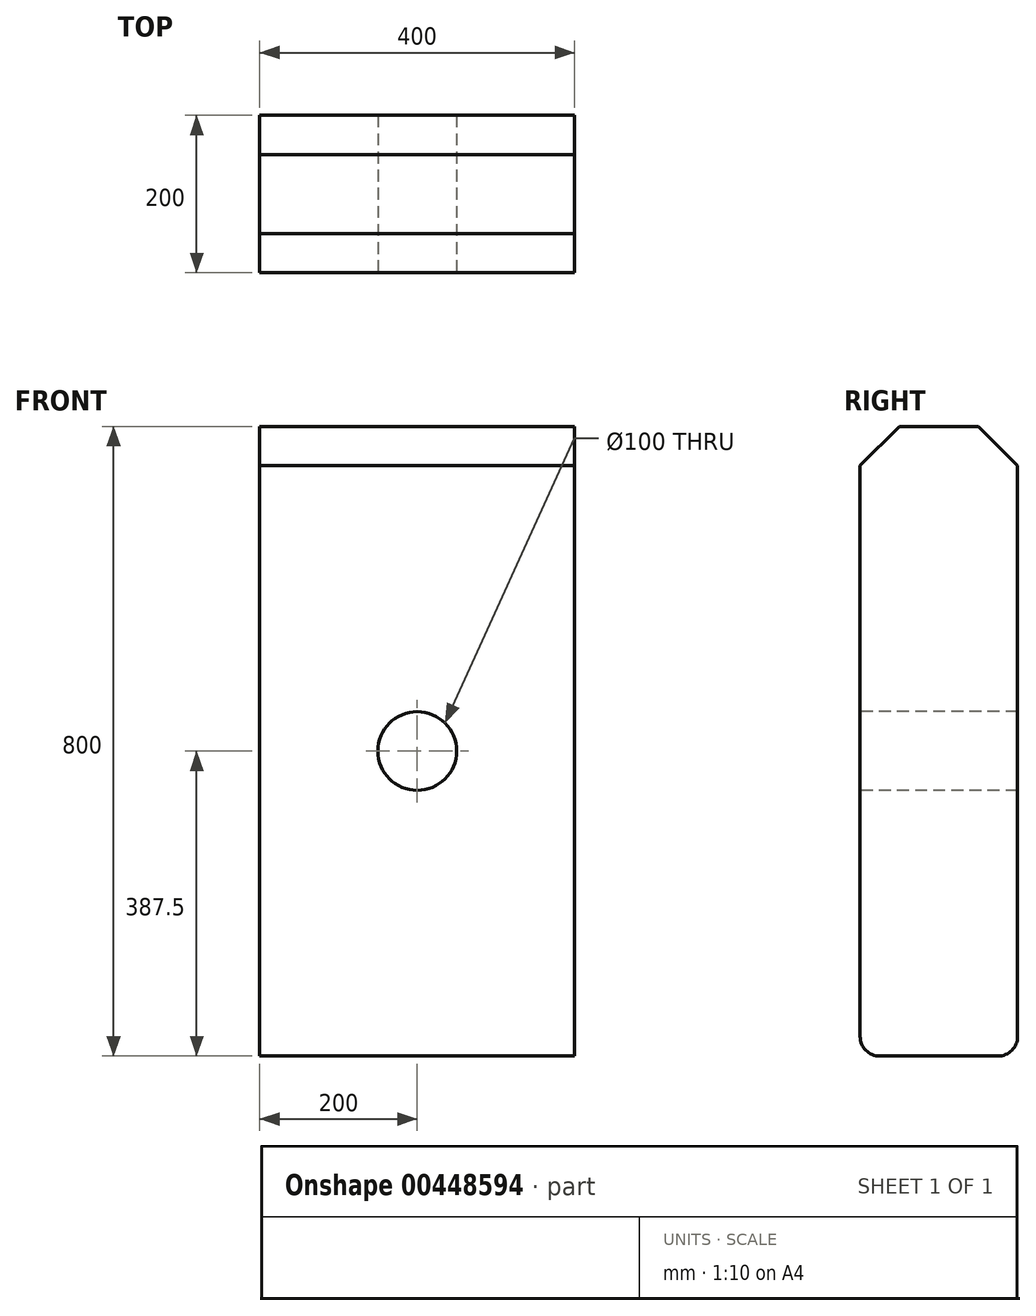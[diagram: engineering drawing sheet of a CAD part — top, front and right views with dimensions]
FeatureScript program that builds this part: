
annotation { "Feature Type Name" : "Feature", "Feature Type Description" : "" }
export const myFeature = defineFeature(function(context is Context, id is Id, definition is map)
    precondition{}
    {
        {
            var Q0;
            Q0=qCreatedBy(makeId("Front.planeOp"),FACE);
            var sketch = newSketch(context, id + "F0", { "sketchPlane" : qUnion([Q0])});
            skLineSegment(sketch, "E0.bottom", {"start": v(0, 0) * mm, "end": v(400, 0) * mm});
            skLineSegment(sketch, "E0.top", {"start": v(0, 800) * mm, "end": v(400, 800) * mm});
            skLineSegment(sketch, "E0.left", {"start": v(0, 0) * mm, "end": v(0, 800) * mm});
            skLineSegment(sketch, "E0.right", {"start": v(400, 0) * mm, "end": v(400, 800) * mm});
            skLineSegment(sketch, "E1.bottom", {"start": v(170.96, 17.79) * mm, "end": v(169.85, 17.79) * mm});
            skLineSegment(sketch, "E1.top", {"start": v(170.96, 0) * mm, "end": v(169.85, 0) * mm});
            skLineSegment(sketch, "E1.left", {"start": v(170.96, 17.79) * mm, "end": v(170.96, 0) * mm});
            skLineSegment(sketch, "E1.right", {"start": v(169.85, 17.79) * mm, "end": v(169.85, 0) * mm});
            skSolve(sketch);
        }
        {
            var Q0;
            Q0=makeQuery(id+"F0.imprint","IMPRINT",FACE,{"disambiguationData":[TD([[makeQuery(id+"F0.imprint","IMPRINT",EDGE,{"derivedFrom":sQuery(id+"F0.wireOp",EDGE,"E1.bottom")}),1.0]])]});
            var Q1;
            Q1=makeQuery(id+"F0.imprint","IMPRINT",FACE,{"disambiguationData":[TD([[makeQuery(id+"F0.imprint","IMPRINT",EDGE,{"derivedFrom":sQuery(id+"F0.wireOp",EDGE,"E0.top")}),-1.0]])]});
            extrude(context, id + "F1", {"entities" : qUnion([Q0, Q1]), "depth" : 200 * mm});
        }
        {
            var Q0;
            Q0=makeQuery(id+"F1.opExtrude","CAP_EDGE",EDGE,{"disambiguationData":[OSD([sQuery(id+"F0.wireOp",EDGE,"E0.top")])],"isStart":false});
            var Q1;
            Q1=makeQuery(id+"F1.opExtrude","CAP_EDGE",EDGE,{"disambiguationData":[OSD([sQuery(id+"F0.wireOp",EDGE,"E0.top")])],"isStart":true});
            chamfer(context, id + "F2", {"entities" : qUnion([Q0, Q1]), "width" : 50 * mm, "tangentPropagation" : true});
        }
        {
            var Q0;
            Q0=makeQuery(id+"F1.opExtrude","CAP_EDGE",EDGE,{"disambiguationData":[OSD([sQuery(id+"F0.wireOp",EDGE,"E0.bottom"),sQuery(id+"F0.wireOp",EDGE,"E1.top")])],"isStart":false});
            var Q1;
            Q1=makeQuery(id+"F1.opExtrude","CAP_EDGE",EDGE,{"disambiguationData":[OSD([sQuery(id+"F0.wireOp",EDGE,"E0.bottom"),sQuery(id+"F0.wireOp",EDGE,"E1.top")])],"isStart":true});
            fillet(context, id + "F3", {"entities" : qUnion([Q0, Q1]), "radius" : 25 * mm, "tangentPropagation" : true, "allowEdgeOverflow" : false});
        }
        {
            var Q0;
            Q0=makeQuery(id+"F1.opExtrude","CAP_FACE",FACE,{"disambiguationData":[OSD([sQuery(id+"F0.wireOp",EDGE,"E0.bottom"),sQuery(id+"F0.wireOp",EDGE,"E0.top"),sQuery(id+"F0.wireOp",EDGE,"E0.left"),sQuery(id+"F0.wireOp",EDGE,"E0.right"),sQuery(id+"F0.wireOp",EDGE,"E1.top")])],"isStart":false});
            var sketch = newSketch(context, id + "F4", { "sketchPlane" : qUnion([Q0])});
            skCircle(sketch, "E2", {"center": v(200, 387.5) * mm, "radius": 50 * mm});
            skPoint(sketch, "E2.centerSnap0", {"position": v(200, 750) * mm});
            skPoint(sketch, "E2.centerSnap1", {"position": v(0, 387.5) * mm});
            skSolve(sketch);
        }
        {
            var Q0;
            Q0=sQuery(id+"F4.wireOp",VERTEX,"E2.center");
            var Q1;
            Q1=makeQuery(id+"F1.opExtrude","SWEPT_BODY",BODY,{"disambiguationData":[OSD([sQuery(id+"F0.wireOp",EDGE,"E0.bottom"),sQuery(id+"F0.wireOp",EDGE,"E0.top"),sQuery(id+"F0.wireOp",EDGE,"E0.left"),sQuery(id+"F0.wireOp",EDGE,"E0.right"),sQuery(id+"F0.wireOp",EDGE,"E1.top")])]});
            hole(context, id + "F5", {"style" : HoleStyle.SIMPLE, "endStyle" : HoleEndStyle.THROUGH, "holeDiameter" : 100 * mm, "isTappedThrough" : true, "tappedDepth" : 12 * mm, "tapClearance" : 3, "locations" : qUnion([Q0]), "scope" : qUnion([Q1])});
        }
    });
